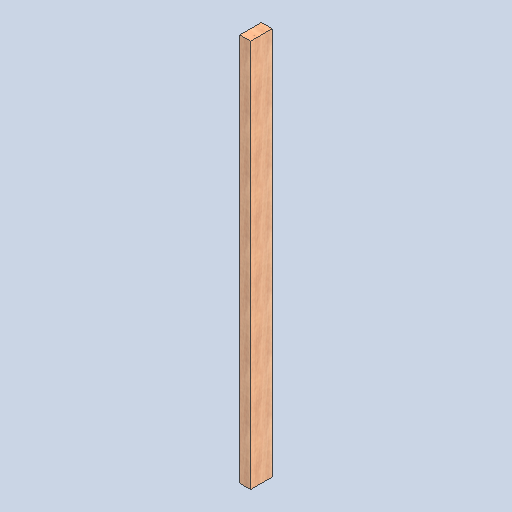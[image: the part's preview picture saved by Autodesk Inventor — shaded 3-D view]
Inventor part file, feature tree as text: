
AUTODESK INVENTOR PART (.ipt)
format: ipt  version: 2025 (Build 290162000, 162)  size: 114,176 bytes
history: native  units: in
note: dims shown in document units (in); Inventor stores cm internally (conversion verified against a paired STEP export)
features: other x3, sketch x1
ambient origin geometry x8: Origin, YZ Plane, XZ Plane, XY Plane, X Axis, Y Axis, Z Axis, Center Point
bodies: Solid1 (feature_tree)
feature tree (4):
  other  "2x4x72.ipt"
  other  "Solid1::2x4x72.ipt"
  other  "TaggingFeature1"
  sketch  "Sketch1"  dims[d0=0.3937in]
